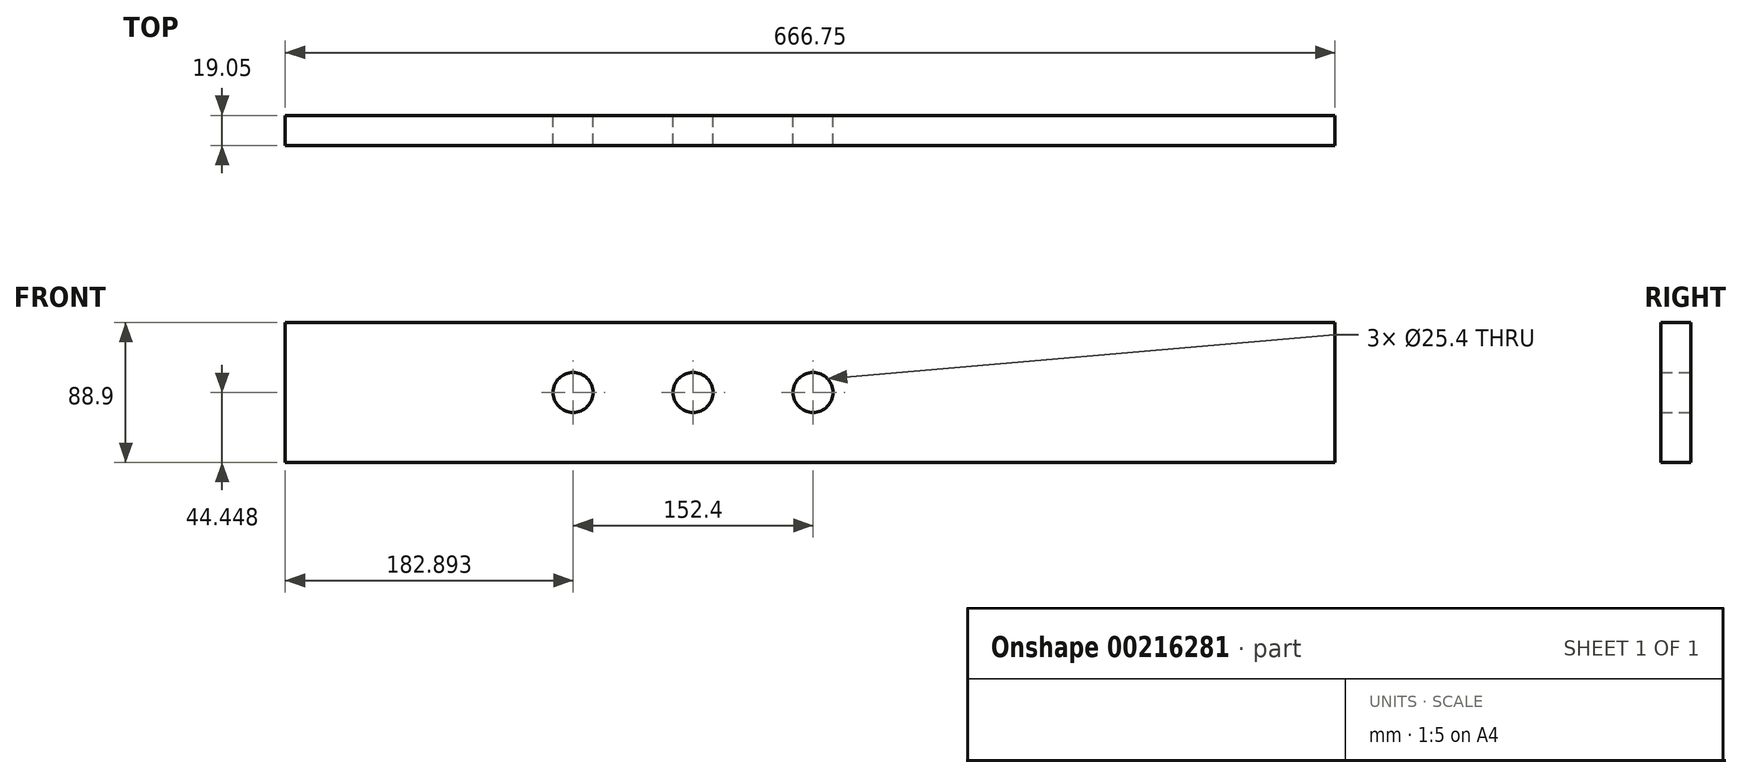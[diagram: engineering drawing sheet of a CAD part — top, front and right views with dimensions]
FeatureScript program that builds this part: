
annotation { "Feature Type Name" : "Feature", "Feature Type Description" : "" }
export const myFeature = defineFeature(function(context is Context, id is Id, definition is map)
    precondition{}
    {
        {
            var Q0;
            Q0=qCreatedBy(makeId("Front.planeOp"),FACE);
            var sketch = newSketch(context, id + "F0", { "sketchPlane" : qUnion([Q0])});
            skLineSegment(sketch, "E0", {"start": v(-619.39, 2068.38) * mm, "end": v(47.36, 2068.38) * mm});
            skLineSegment(sketch, "E1", {"start": v(47.36, 2068.38) * mm, "end": v(47.36, 2157.28) * mm});
            skLineSegment(sketch, "E2", {"start": v(47.36, 2157.28) * mm, "end": v(-619.39, 2157.28) * mm});
            skLineSegment(sketch, "E3", {"start": v(-619.39, 2157.28) * mm, "end": v(-619.39, 2068.38) * mm});
            skCircle(sketch, "E4", {"center": v(-436.5, 2112.83) * mm, "radius": 12.7 * mm});
            skCircle(sketch, "E5", {"center": v(-360.3, 2112.83) * mm, "radius": 12.7 * mm});
            skCircle(sketch, "E6", {"center": v(-284.1, 2112.83) * mm, "radius": 12.7 * mm});
            skLineSegment(sketch, "E7", {"start": v(-619.39, 2112.83) * mm, "end": v(47.36, 2112.83) * mm, "construction": true});
            skSolve(sketch);
        }
        {
            var Q0;
            Q0=makeQuery(id+"F0.imprint","IMPRINT",FACE,{"disambiguationData":[TD([[makeQuery(id+"F0.imprint","IMPRINT",EDGE,{"derivedFrom":sQuery(id+"F0.wireOp",EDGE,"E0")}),1.0]])]});
            extrude(context, id + "F1", {"entities" : qUnion([Q0]), "depth" : 19.05 * mm});
        }
    });
